# Revit family: Electronics_Commercial-Audio_Biamp_Volume-Control_D-VOL30_D-VOL60_D-VOL120
name_source: partatom
category: Communication Devices
units: mm (PartAtom-declared; Revit-internal decimal feet)

## family parameters
Cut with Voids When Loaded = No
Host = Face
Maintain Annotation Orientation = No
OmniClass Number = 23.85.10.11.14
OmniClass Title = Audio Equipment
Part Type = Normal
Room Calculation Point = No
Round Connector Dimension = Use Diameter
Shared = No

## types (3) — shared parameters
Default Elevation = 4' - 0"
Depth = 0' - 2"
Height = 0' - 4 1/2"
Housing Material = Biamp - Plastic - White
Manufacturer = Biamp
Mounting = Screw
Product Documentation Link = https://downloads.biamp.com
Product Page URL = https://www.biamp.com
Product data url = https://www.bimobject.com
Steps = 0 + 11
Stereo/mono = mono
URL = https://www.biamp.com
Width = 0' - 3"

## per-type parameters (varying)
| type | Description | Weight |
| D-VOL30 | D-VOL30 70 Volt, 30 Watts Volume Controls Decora Style | 0.37 kgf |
| D-VOL60 | D-VOL60 70 Volt, 60 Watts Volume Controls Decora Style | 0.41 kgf |
| D-VOL120 | D-VOL120 70 Volt, 120 Watts Volume Controls Decora Style | 0.41 kgf |

note: column(s) folded — value = type name in every type: Model

## geometry (parser evidence)
native form markers: Sweep x2
no freeform markers — native parametric forms only
